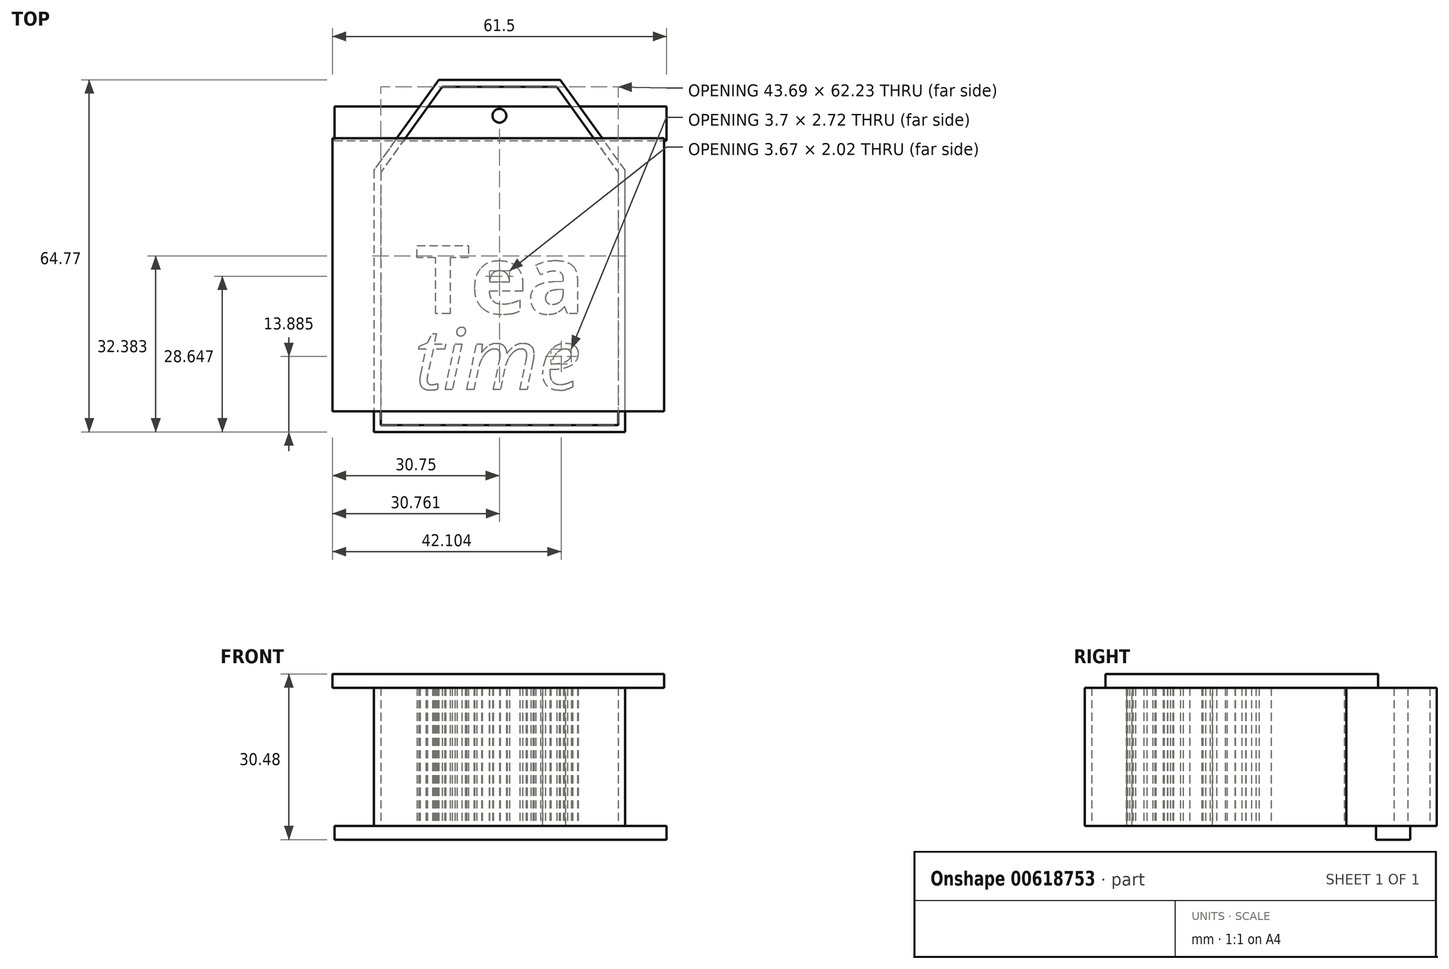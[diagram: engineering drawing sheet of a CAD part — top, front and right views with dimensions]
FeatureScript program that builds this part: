
annotation { "Feature Type Name" : "Feature", "Feature Type Description" : "" }
export const myFeature = defineFeature(function(context is Context, id is Id, definition is map)
    precondition{}
    {
        {
            var Q0;
            Q0=qCreatedBy(makeId("Top.planeOp"),FACE);
            var sketch = newSketch(context, id + "F0", { "sketchPlane" : qUnion([Q0])});
            skLineSegment(sketch, "E0", {"start": v(0, 44.42) * mm, "end": v(-10.54, 44.42) * mm});
            skLineSegment(sketch, "E1", {"start": v(-10.54, 44.42) * mm, "end": v(-21.84, 28.67) * mm});
            skLineSegment(sketch, "E2", {"start": v(-21.84, 28.67) * mm, "end": v(-21.84, -17.81) * mm});
            skLineSegment(sketch, "E3", {"start": v(-21.84, -17.81) * mm, "end": v(0, -17.81) * mm});
            skLineSegment(sketch, "E4.MirrorCS", {"start": v(0, 44.42) * mm, "end": v(10.54, 44.42) * mm});
            skLineSegment(sketch, "E5.MirrorCS", {"start": v(10.54, 44.42) * mm, "end": v(21.84, 28.67) * mm});
            skLineSegment(sketch, "E6.MirrorCS", {"start": v(21.84, 28.67) * mm, "end": v(21.84, -17.81) * mm});
            skLineSegment(sketch, "E7.MirrorCS", {"start": v(21.84, -17.81) * mm, "end": v(0, -17.81) * mm});
            skLineSegment(sketch, "E8", {"start": v(-23.11, 29.08) * mm, "end": v(-23.11, -19.08) * mm});
            skLineSegment(sketch, "E9", {"start": v(-23.11, -19.08) * mm, "end": v(23.11, -19.08) * mm});
            skLineSegment(sketch, "E10", {"start": v(23.11, -19.08) * mm, "end": v(23.11, 29.08) * mm});
            skLineSegment(sketch, "E11", {"start": v(23.11, 29.08) * mm, "end": v(11.2, 45.69) * mm});
            skLineSegment(sketch, "E12", {"start": v(11.2, 45.69) * mm, "end": v(-11.2, 45.69) * mm});
            skLineSegment(sketch, "E13", {"start": v(-11.2, 45.69) * mm, "end": v(-23.11, 29.08) * mm});
            skSolve(sketch);
        }
        {
            var Q0;
            Q0=makeQuery(id+"F0.imprint","IMPRINT",FACE,{"disambiguationData":[TD([[makeQuery(id+"F0.imprint","IMPRINT",EDGE,{"derivedFrom":sQuery(id+"F0.wireOp",EDGE,"E0")}),-1.0]])]});
            extrude(context, id + "F1", {"entities" : qUnion([Q0]), "depth" : 25.4 * mm, "offsetDistance" : 25.4 * mm});
        }
        {
            var Q0;
            Q0=qCreatedBy(makeId("Top.planeOp"),FACE);
            var sketch = newSketch(context, id + "F2", { "sketchPlane" : qUnion([Q0])});
            skCircle(sketch, "E14", {"center": v(0, 39.08) * mm, "radius": 1.27 * mm});
            skSolve(sketch);
        }
        {
            var Q0;
            Q0 = qSketchRegion(id + "F2", true);
            extrude(context, id + "F3", {"entities" : qUnion([Q0]), "depth" : 25.4 * mm, "offsetDistance" : 25.4 * mm});
        }
        {
            var Q0;
            Q0=makeQuery(id+"F1.opExtrude","CAP_FACE",FACE,{"disambiguationData":[OSD([sQuery(id+"F0.wireOp",EDGE,"E0"),sQuery(id+"F0.wireOp",EDGE,"E1"),sQuery(id+"F0.wireOp",EDGE,"E2"),sQuery(id+"F0.wireOp",EDGE,"E3"),sQuery(id+"F0.wireOp",EDGE,"E4.MirrorCS"),sQuery(id+"F0.wireOp",EDGE,"E5.MirrorCS"),sQuery(id+"F0.wireOp",EDGE,"E6.MirrorCS"),sQuery(id+"F0.wireOp",EDGE,"E7.MirrorCS"),sQuery(id+"F0.wireOp",EDGE,"E8"),sQuery(id+"F0.wireOp",EDGE,"E9"),sQuery(id+"F0.wireOp",EDGE,"E10"),sQuery(id+"F0.wireOp",EDGE,"E11"),sQuery(id+"F0.wireOp",EDGE,"E12"),sQuery(id+"F0.wireOp",EDGE,"E13")])],"isStart":true});
            var sketch = newSketch(context, id + "F4", { "sketchPlane" : qUnion([Q0])});
            skLineSegment(sketch, "E15.bottom", {"start": v(-30.33, -34.51) * mm, "end": v(30.75, -34.51) * mm});
            skLineSegment(sketch, "E15.top", {"start": v(-30.33, -40.79) * mm, "end": v(30.75, -40.79) * mm});
            skLineSegment(sketch, "E15.left", {"start": v(-30.33, -34.51) * mm, "end": v(-30.33, -40.79) * mm});
            skLineSegment(sketch, "E15.right", {"start": v(30.75, -34.51) * mm, "end": v(30.75, -40.79) * mm});
            skSolve(sketch);
        }
        {
            var Q0;
            Q0 = qSketchRegion(id + "F4", true);
            extrude(context, id + "F5", {"entities" : qUnion([Q0]), "depth" : 2.54 * mm, "offsetDistance" : 25.4 * mm});
        }
        {
            var Q0;
            Q0=qCreatedBy(makeId("Top.planeOp"),FACE);
            var sketch = newSketch(context, id + "F6", { "sketchPlane" : qUnion([Q0])});
            skText(sketch, "E16", { "text": "Tea", "fontName": "OpenSans-Bold.ttf"});
            const initialGuessF6  = {"E16": [-0.0155, 0.00267, 1, 0, 0.01265]};
            skSetInitialGuess(sketch, initialGuessF6);
            skSolve(sketch);
        }
        {
            var Q0;
            Q0=qCreatedBy(makeId("Top.planeOp"),FACE);
            var sketch = newSketch(context, id + "F7", { "sketchPlane" : qUnion([Q0])});
            skText(sketch, "E17", { "text": "time", "fontName": "OpenSans-Italic.ttf"});
            const initialGuessF7  = {"E17": [-0.0155, -0.01128, 1, 0, 0.01128]};
            skSetInitialGuess(sketch, initialGuessF7);
            skSolve(sketch);
        }
        {
            var Q0;
            Q0 = qSketchRegion(id + "F6", true);
            var Q1;
            Q1 = qSketchRegion(id + "F7", true);
            extrude(context, id + "F8", {"entities" : qUnion([Q0, Q1]), "depth" : 25.4 * mm, "offsetDistance" : 25.4 * mm});
        }
        {
            var Q0;
            Q0=makeQuery(id+"F1.opExtrude","CAP_FACE",FACE,{"disambiguationData":[OSD([sQuery(id+"F0.wireOp",EDGE,"E0"),sQuery(id+"F0.wireOp",EDGE,"E1"),sQuery(id+"F0.wireOp",EDGE,"E2"),sQuery(id+"F0.wireOp",EDGE,"E3"),sQuery(id+"F0.wireOp",EDGE,"E4.MirrorCS"),sQuery(id+"F0.wireOp",EDGE,"E5.MirrorCS"),sQuery(id+"F0.wireOp",EDGE,"E6.MirrorCS"),sQuery(id+"F0.wireOp",EDGE,"E7.MirrorCS"),sQuery(id+"F0.wireOp",EDGE,"E8"),sQuery(id+"F0.wireOp",EDGE,"E9"),sQuery(id+"F0.wireOp",EDGE,"E10"),sQuery(id+"F0.wireOp",EDGE,"E11"),sQuery(id+"F0.wireOp",EDGE,"E12"),sQuery(id+"F0.wireOp",EDGE,"E13")])],"isStart":false});
            var sketch = newSketch(context, id + "F9", { "sketchPlane" : qUnion([Q0])});
            skLineSegment(sketch, "E18.bottom", {"start": v(-30.75, 34.93) * mm, "end": v(30.33, 34.93) * mm});
            skLineSegment(sketch, "E18.top", {"start": v(-30.75, -15.27) * mm, "end": v(30.33, -15.27) * mm});
            skLineSegment(sketch, "E18.left", {"start": v(-30.75, 34.93) * mm, "end": v(-30.75, -15.27) * mm});
            skLineSegment(sketch, "E18.right", {"start": v(30.33, 34.93) * mm, "end": v(30.33, -15.27) * mm});
            skSolve(sketch);
        }
        {
            var Q0;
            Q0 = qSketchRegion(id + "F9", true);
            extrude(context, id + "F10", {"entities" : qUnion([Q0]), "depth" : 2.54 * mm, "offsetDistance" : 25.4 * mm});
        }
    });
